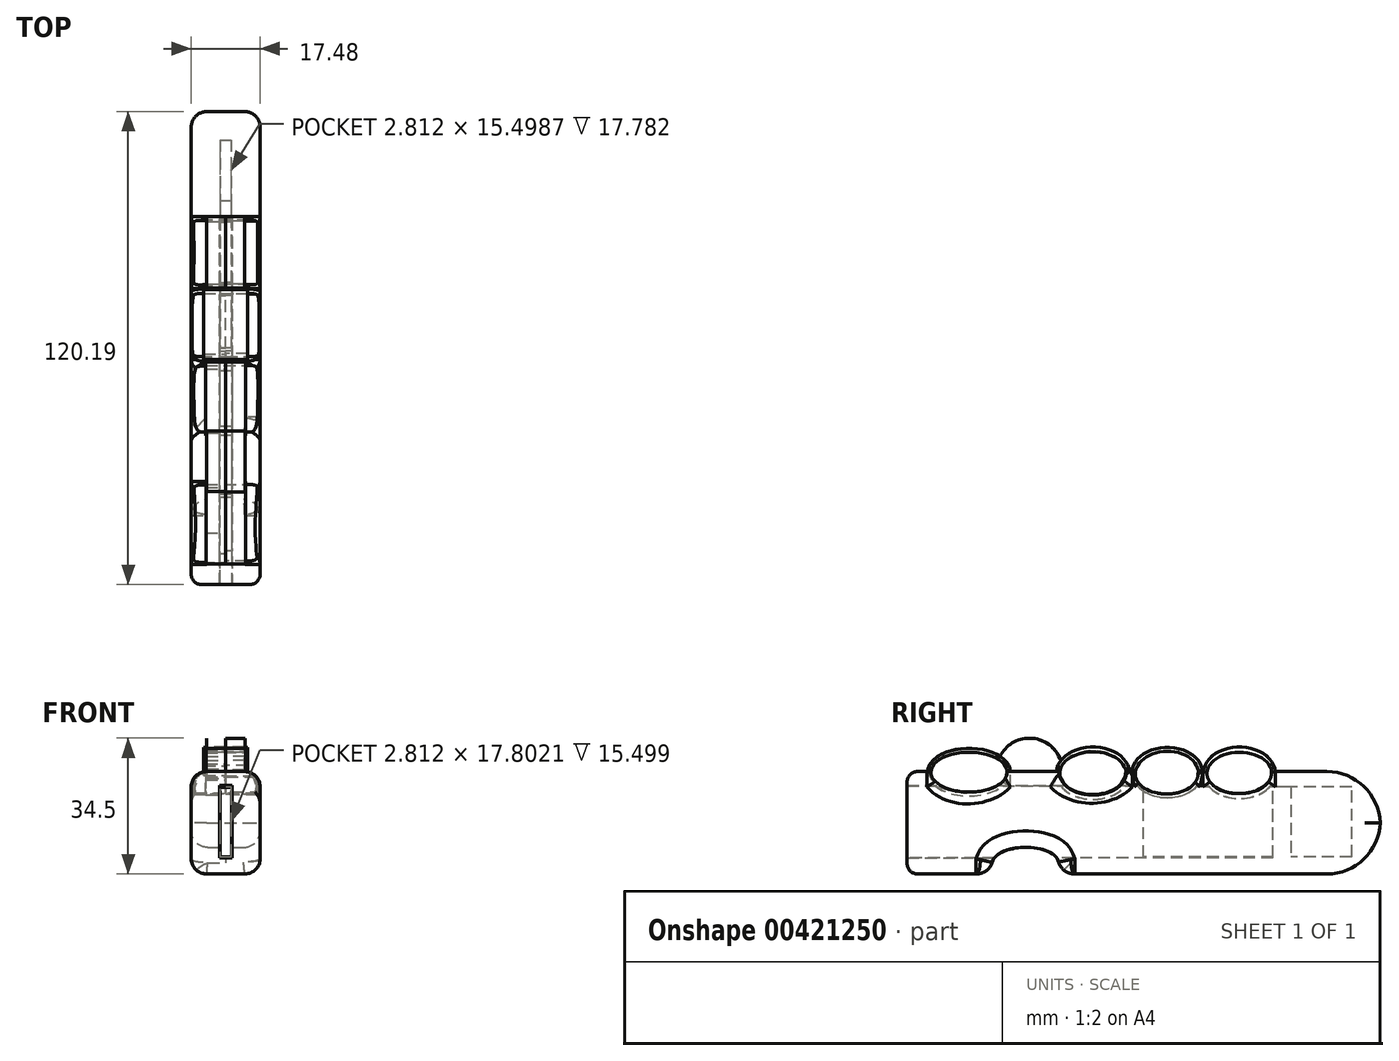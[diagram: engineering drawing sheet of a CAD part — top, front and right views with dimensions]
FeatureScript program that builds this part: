
annotation { "Feature Type Name" : "Feature", "Feature Type Description" : "" }
export const myFeature = defineFeature(function(context is Context, id is Id, definition is map)
    precondition{}
    {
        {
            var Q0;
            Q0=qCreatedBy(makeId("Top.planeOp"),FACE);
            var sketch = newSketch(context, id + "F0", { "sketchPlane" : qUnion([Q0])});
            skLineSegment(sketch, "E0.bottom", {"start": v(8.74, -60.1) * mm, "end": v(-8.74, -60.1) * mm});
            skLineSegment(sketch, "E0.top", {"start": v(8.74, 60.1) * mm, "end": v(-8.74, 60.1) * mm});
            skLineSegment(sketch, "E0.left", {"start": v(8.74, -60.1) * mm, "end": v(8.74, 60.1) * mm});
            skLineSegment(sketch, "E0.right", {"start": v(-8.74, -60.1) * mm, "end": v(-8.74, 60.1) * mm});
            skPoint(sketch, "E0.middle", {"position": v(0, 0) * mm});
            skSolve(sketch);
        }
        {
            var Q0;
            Q0=makeQuery(id+"F0.imprint","IMPRINT",FACE,{"disambiguationData":[TD([[makeQuery(id+"F0.imprint","IMPRINT",EDGE,{"derivedFrom":sQuery(id+"F0.wireOp",EDGE,"E0.bottom")}),-1.0]])]});
            extrude(context, id + "F1", {"entities" : qUnion([Q0]), "depth" : 26 * mm});
        }
        {
            var Q0;
            Q0=makeQuery(id+"F1.opExtrude","SWEPT_EDGE",EDGE,{"disambiguationData":[OSD([sQuery(id+"F0.wireOp",EDGE,"E0.bottom"),sQuery(id+"F0.wireOp",EDGE,"E0.left")])]});
            var Q1;
            Q1=makeQuery(id+"F1.opExtrude","SWEPT_EDGE",EDGE,{"disambiguationData":[OSD([sQuery(id+"F0.wireOp",EDGE,"E0.bottom"),sQuery(id+"F0.wireOp",EDGE,"E0.right")])]});
            var Q2;
            Q2=makeQuery(id+"F1.opExtrude","CAP_EDGE",EDGE,{"disambiguationData":[OSD([sQuery(id+"F0.wireOp",EDGE,"E0.bottom")])],"isStart":true});
            var Q3;
            Q3=makeQuery(id+"F1.opExtrude","CAP_EDGE",EDGE,{"disambiguationData":[OSD([sQuery(id+"F0.wireOp",EDGE,"E0.bottom")])],"isStart":false});
            fillet(context, id + "F2", {"entities" : qUnion([Q0, Q1, Q2, Q3]), "radius" : 2.66 * mm, "tangentPropagation" : true, "allowEdgeOverflow" : false});
        }
        {
            var Q0;
            Q0=makeQuery(id+"F1.opExtrude","SWEPT_FACE",FACE,{"disambiguationData":[OSD([sQuery(id+"F0.wireOp",EDGE,"E0.bottom")])]});
            var sketch = newSketch(context, id + "F3", { "sketchPlane" : qUnion([Q0])});
            skLineSegment(sketch, "E1.bottom", {"start": v(1.46, 22.1) * mm, "end": v(-1.46, 22.1) * mm});
            skLineSegment(sketch, "E1.top", {"start": v(1.46, 4.26) * mm, "end": v(-1.46, 4.26) * mm});
            skLineSegment(sketch, "E1.left", {"start": v(1.46, 22.1) * mm, "end": v(1.46, 4.26) * mm});
            skLineSegment(sketch, "E1.right", {"start": v(-1.46, 22.1) * mm, "end": v(-1.46, 4.26) * mm});
            skPoint(sketch, "E1.middle", {"position": v(0, 13.18) * mm});
            skSolve(sketch);
        }
        {
            var Q0;
            Q0=makeQuery(id+"F1.opExtrude","CAP_EDGE",EDGE,{"disambiguationData":[OSD([sQuery(id+"F0.wireOp",EDGE,"E0.top")])],"isStart":false});
            var Q1;
            Q1=makeQuery(id+"F1.opExtrude","CAP_EDGE",EDGE,{"disambiguationData":[OSD([sQuery(id+"F0.wireOp",EDGE,"E0.top")])],"isStart":true});
            fillet(context, id + "F4", {"entities" : qUnion([Q0, Q1]), "radius" : 13.52 * mm, "tangentPropagation" : true, "allowEdgeOverflow" : false});
        }
        {
            var Q0;
            Q0=makeQuery(id+"F4.opFillet","BLEND_EDGE",EDGE,{"blendedFrom":[makeQuery(id+"F1.opExtrude","CAP_EDGE",EDGE,{"disambiguationData":[OSD([sQuery(id+"F0.wireOp",EDGE,"E0.top")])],"isStart":true}),makeQuery(id+"F1.opExtrude","SWEPT_FACE",FACE,{"disambiguationData":[OSD([sQuery(id+"F0.wireOp",EDGE,"E0.right")])]})],"blendedInto":[makeQuery(id+"F1.opExtrude","SWEPT_FACE",FACE,{"disambiguationData":[OSD([sQuery(id+"F0.wireOp",EDGE,"E0.right")])]})]});
            var Q1;
            Q1=makeQuery(id+"F4.opFillet","BLEND_EDGE",EDGE,{"blendedFrom":[makeQuery(id+"F1.opExtrude","CAP_EDGE",EDGE,{"disambiguationData":[OSD([sQuery(id+"F0.wireOp",EDGE,"E0.top")])],"isStart":false}),makeQuery(id+"F1.opExtrude","SWEPT_FACE",FACE,{"disambiguationData":[OSD([sQuery(id+"F0.wireOp",EDGE,"E0.right")])]})],"blendedInto":[makeQuery(id+"F1.opExtrude","SWEPT_FACE",FACE,{"disambiguationData":[OSD([sQuery(id+"F0.wireOp",EDGE,"E0.right")])]})]});
            var Q2;
            Q2=makeQuery(id+"F4.opFillet","BLEND_EDGE",EDGE,{"blendedFrom":[makeQuery(id+"F1.opExtrude","CAP_EDGE",EDGE,{"disambiguationData":[OSD([sQuery(id+"F0.wireOp",EDGE,"E0.top")])],"isStart":false}),makeQuery(id+"F1.opExtrude","SWEPT_FACE",FACE,{"disambiguationData":[OSD([sQuery(id+"F0.wireOp",EDGE,"E0.left")])]})],"blendedInto":[makeQuery(id+"F1.opExtrude","SWEPT_FACE",FACE,{"disambiguationData":[OSD([sQuery(id+"F0.wireOp",EDGE,"E0.left")])]})]});
            var Q3;
            Q3=makeQuery(id+"F4.opFillet","BLEND_EDGE",EDGE,{"blendedFrom":[makeQuery(id+"F1.opExtrude","CAP_EDGE",EDGE,{"disambiguationData":[OSD([sQuery(id+"F0.wireOp",EDGE,"E0.top")])],"isStart":true}),makeQuery(id+"F1.opExtrude","SWEPT_FACE",FACE,{"disambiguationData":[OSD([sQuery(id+"F0.wireOp",EDGE,"E0.left")])]})],"blendedInto":[makeQuery(id+"F1.opExtrude","SWEPT_FACE",FACE,{"disambiguationData":[OSD([sQuery(id+"F0.wireOp",EDGE,"E0.left")])]})]});
            fillet(context, id + "F5", {"entities" : qUnion([Q0, Q1, Q2, Q3]), "radius" : 3.86 * mm, "tangentPropagation" : true, "allowEdgeOverflow" : false});
        }
        {
            var Q0;
            Q0=qCreatedBy(makeId("Right.planeOp"),FACE);
            var sketch = newSketch(context, id + "F6", { "sketchPlane" : qUnion([Q0])});
            skFitSpline(sketch, "E2", {"points": [v(-37.07, 26.03) * mm, v(-44.76, 21.99) * mm, v(-51.63, 25.96) * mm, v(-37.07, 26.03) * mm]});
            skSolve(sketch);
        }
        {
            var Q0;
            Q0=qCreatedBy(makeId("Right.planeOp"),FACE);
            var sketch = newSketch(context, id + "F7", { "sketchPlane" : qUnion([Q0])});
            skFitSpline(sketch, "E3", {"points": [v(-37.02, 26.06) * mm, v(-44.82, 21.98) * mm, v(-51.63, 25.93) * mm, v(-37.02, 26.06) * mm]});
            skSolve(sketch);
        }
        {
            var Q0;
            Q0 = qSketchRegion(id + "F6", true);
            extrude(context, id + "F8", {"entities" : qUnion([Q0]), "operationType" : NewBodyOperationType.REMOVE, "oppositeDirection" : true, "depth" : 25 * mm});
        }
        {
            var Q0;
            Q0 = qSketchRegion(id + "F7", true);
            extrude(context, id + "F9", {"entities" : qUnion([Q0]), "operationType" : NewBodyOperationType.REMOVE, "depth" : 25 * mm});
        }
        {
            var Q0;
            {var subQ0=sQuery(id+"F0.wireOp",EDGE,"E0.right");Q0=makeQuery(id+"F8.boolean.opBoolean","INTERSECT",EDGE,{"disambiguationData":[OD(0.0)],"derivedFrom":[makeQuery(id+"F5.opFillet","BLEND_FACE",FACE,{"disambiguationData":[OSD([subQ0]),TDD([makeQuery(id+"F1.opExtrude","CAP_EDGE",EDGE,{"disambiguationData":[OSD([subQ0])],"isStart":false})])]}),makeQuery(id+"F8.opExtrude","SWEPT_FACE",FACE,{"disambiguationData":[OSD([sQuery(id+"F6.wireOp",EDGE,"E2")])]})]});}
            var Q1;
            {var subQ0=sQuery(id+"F0.wireOp",EDGE,"E0.right");Q1=makeQuery(id+"F8.boolean.opBoolean","INTERSECT",EDGE,{"disambiguationData":[OD(1.0)],"derivedFrom":[makeQuery(id+"F5.opFillet","BLEND_FACE",FACE,{"disambiguationData":[OSD([subQ0]),TDD([makeQuery(id+"F1.opExtrude","CAP_EDGE",EDGE,{"disambiguationData":[OSD([subQ0])],"isStart":false})])]}),makeQuery(id+"F8.opExtrude","SWEPT_FACE",FACE,{"disambiguationData":[OSD([sQuery(id+"F6.wireOp",EDGE,"E2")])]})]});}
            fillet(context, id + "F10", {"entities" : qUnion([Q0, Q1]), "radius" : 4.2 * mm, "tangentPropagation" : true, "allowEdgeOverflow" : false});
        }
        {
            var Q0;
            {var subQ0=sQuery(id+"F0.wireOp",EDGE,"E0.left");Q0=makeQuery(id+"F9.boolean.opBoolean","INTERSECT",EDGE,{"disambiguationData":[OD(1.0)],"derivedFrom":[makeQuery(id+"F5.opFillet","BLEND_FACE",FACE,{"disambiguationData":[OSD([subQ0]),TDD([makeQuery(id+"F1.opExtrude","CAP_EDGE",EDGE,{"disambiguationData":[OSD([subQ0])],"isStart":false})])]}),makeQuery(id+"F9.opExtrude","SWEPT_FACE",FACE,{"disambiguationData":[OSD([sQuery(id+"F7.wireOp",EDGE,"E3")])]})]});}
            var Q1;
            {var subQ0=sQuery(id+"F0.wireOp",EDGE,"E0.left");Q1=makeQuery(id+"F9.boolean.opBoolean","INTERSECT",EDGE,{"disambiguationData":[OD(0.0)],"derivedFrom":[makeQuery(id+"F5.opFillet","BLEND_FACE",FACE,{"disambiguationData":[OSD([subQ0]),TDD([makeQuery(id+"F1.opExtrude","CAP_EDGE",EDGE,{"disambiguationData":[OSD([subQ0])],"isStart":false})])]}),makeQuery(id+"F9.opExtrude","SWEPT_FACE",FACE,{"disambiguationData":[OSD([sQuery(id+"F7.wireOp",EDGE,"E3")])]})]});}
            fillet(context, id + "F11", {"entities" : qUnion([Q0, Q1]), "radius" : 4.2 * mm, "tangentPropagation" : true, "allowEdgeOverflow" : false});
        }
        {
            var Q0;
            Q0=makeQuery(id+"F3.imprint","IMPRINT",FACE,{"disambiguationData":[TD([[makeQuery(id+"F3.imprint","IMPRINT",EDGE,{"derivedFrom":sQuery(id+"F3.wireOp",EDGE,"E1.bottom")}),-1.0]])]});
            var sketch = newSketch(context, id + "F12", { "sketchPlane" : qUnion([Q0])});
            skLineSegment(sketch, "E4.bottom", {"start": v(-1.6, 4.04) * mm, "end": v(1.6, 4.04) * mm});
            skLineSegment(sketch, "E4.top", {"start": v(-1.6, 22.35) * mm, "end": v(1.6, 22.35) * mm});
            skLineSegment(sketch, "E4.left", {"start": v(-1.6, 4.04) * mm, "end": v(-1.6, 22.35) * mm});
            skLineSegment(sketch, "E4.right", {"start": v(1.6, 4.04) * mm, "end": v(1.6, 22.35) * mm});
            skPoint(sketch, "E4.middle", {"position": v(0, 13.2) * mm});
            skSolve(sketch);
        }
        {
            var Q0;
            Q0 = qSketchRegion(id + "F12", true);
            extrude(context, id + "F13", {"entities" : qUnion([Q0]), "operationType" : NewBodyOperationType.REMOVE, "oppositeDirection" : true, "depth" : 93 * mm});
        }
        {
            var Q0;
            Q0=makeQuery(id+"F3.imprint","IMPRINT",FACE,{"disambiguationData":[TD([[makeQuery(id+"F3.imprint","IMPRINT",EDGE,{"derivedFrom":sQuery(id+"F3.wireOp",EDGE,"E1.bottom")}),1.0]])]});
            var sketch = newSketch(context, id + "F14", { "sketchPlane" : qUnion([Q0])});
            skLineSegment(sketch, "E5.bottom", {"start": v(-1.4, 4.37) * mm, "end": v(1.4, 4.37) * mm});
            skLineSegment(sketch, "E5.top", {"start": v(-1.4, 22.17) * mm, "end": v(1.4, 22.17) * mm});
            skLineSegment(sketch, "E5.left", {"start": v(-1.4, 4.37) * mm, "end": v(-1.4, 22.17) * mm});
            skLineSegment(sketch, "E5.right", {"start": v(1.4, 4.37) * mm, "end": v(1.4, 22.17) * mm});
            skPoint(sketch, "E5.middle", {"position": v(0, 13.27) * mm});
            skSolve(sketch);
        }
        {
            var Q0;
            Q0 = qSketchRegion(id + "F14", true);
            extrude(context, id + "F15", {"entities" : qUnion([Q0]), "operationType" : NewBodyOperationType.REMOVE, "oppositeDirection" : true, "depth" : 113 * mm});
        }
        {
            var Q0;
            Q0=qCreatedBy(makeId("Right.planeOp"),FACE);
            var sketch = newSketch(context, id + "F16", { "sketchPlane" : qUnion([Q0])});
            skFitSpline(sketch, "E6", {"points": [v(-21.94, 3.88) * mm, v(-30.28, -6.1) * mm, v(-38.08, 3.82) * mm, v(-21.94, 3.88) * mm]});
            skSolve(sketch);
        }
        {
            var Q0;
            Q0=qCreatedBy(makeId("Right.planeOp"),FACE);
            var sketch = newSketch(context, id + "F17", { "sketchPlane" : qUnion([Q0])});
            skFitSpline(sketch, "E7", {"points": [v(-21.92, 3.9) * mm, v(-30.28, -6.09) * mm, v(-38.07, 3.82) * mm, v(-21.92, 3.9) * mm]});
            skSolve(sketch);
        }
        {
            var Q0;
            Q0 = qSketchRegion(id + "F17", true);
            extrude(context, id + "F18", {"entities" : qUnion([Q0]), "operationType" : NewBodyOperationType.REMOVE, "oppositeDirection" : true, "depth" : 25 * mm});
        }
        {
            var Q0;
            Q0 = qSketchRegion(id + "F16", true);
            extrude(context, id + "F19", {"entities" : qUnion([Q0]), "operationType" : NewBodyOperationType.REMOVE, "depth" : 25 * mm});
        }
        {
            var Q0;
            Q0=makeQuery(id+"F18.boolean.opBoolean","INTERSECT",EDGE,{"derivedFrom":[makeQuery(id+"F1.opExtrude","SWEPT_FACE",FACE,{"disambiguationData":[OSD([sQuery(id+"F0.wireOp",EDGE,"E0.right")])]}),makeQuery(id+"F18.opExtrude","SWEPT_FACE",FACE,{"disambiguationData":[OSD([sQuery(id+"F17.wireOp",EDGE,"E7")])]})]});
            var Q1;
            Q1=makeQuery(id+"F19.boolean.opBoolean","INTERSECT",EDGE,{"derivedFrom":[makeQuery(id+"F1.opExtrude","SWEPT_FACE",FACE,{"disambiguationData":[OSD([sQuery(id+"F0.wireOp",EDGE,"E0.left")])]}),makeQuery(id+"F19.opExtrude","SWEPT_FACE",FACE,{"disambiguationData":[OSD([sQuery(id+"F16.wireOp",EDGE,"E6")])]})]});
            fillet(context, id + "F20", {"entities" : qUnion([Q0, Q1]), "radius" : 4.2 * mm, "allowEdgeOverflow" : false});
        }
        {
            var Q0;
            Q0=makeQuery(id+"F18.boolean.opBoolean","INTERSECT",EDGE,{"disambiguationData":[OD(0.0)],"derivedFrom":[makeQuery(id+"F1.opExtrude","CAP_FACE",FACE,{"disambiguationData":[OSD([sQuery(id+"F0.wireOp",EDGE,"E0.bottom"),sQuery(id+"F0.wireOp",EDGE,"E0.top"),sQuery(id+"F0.wireOp",EDGE,"E0.left"),sQuery(id+"F0.wireOp",EDGE,"E0.right")])],"isStart":true}),makeQuery(id+"F18.opExtrude","SWEPT_FACE",FACE,{"disambiguationData":[OSD([sQuery(id+"F17.wireOp",EDGE,"E7")])]})]});
            var Q1;
            Q1=makeQuery(id+"F19.boolean.opBoolean","INTERSECT",EDGE,{"disambiguationData":[OD(1.0)],"derivedFrom":[makeQuery(id+"F1.opExtrude","CAP_FACE",FACE,{"disambiguationData":[OSD([sQuery(id+"F0.wireOp",EDGE,"E0.bottom"),sQuery(id+"F0.wireOp",EDGE,"E0.top"),sQuery(id+"F0.wireOp",EDGE,"E0.left"),sQuery(id+"F0.wireOp",EDGE,"E0.right")])],"isStart":true}),makeQuery(id+"F19.opExtrude","SWEPT_FACE",FACE,{"disambiguationData":[OSD([sQuery(id+"F16.wireOp",EDGE,"E6")])]})]});
            fillet(context, id + "F21", {"entities" : qUnion([Q0, Q1]), "radius" : 4.2 * mm, "tangentPropagation" : true, "allowEdgeOverflow" : false});
        }
        {
            var Q0;
            Q0=qCreatedBy(makeId("Right.planeOp"),FACE);
            var sketch = newSketch(context, id + "F22", { "sketchPlane" : qUnion([Q0])});
            skLineSegment(sketch, "E8.bottom", {"start": v(-37.4, 24.67) * mm, "end": v(-20.56, 24.67) * mm});
            skLineSegment(sketch, "E8.top", {"start": v(-37.4, 34.49) * mm, "end": v(-20.56, 34.49) * mm});
            skLineSegment(sketch, "E8.left", {"start": v(-37.4, 24.67) * mm, "end": v(-37.4, 34.49) * mm});
            skLineSegment(sketch, "E8.right", {"start": v(-20.56, 24.67) * mm, "end": v(-20.56, 34.49) * mm});
            skPoint(sketch, "E8.middle", {"position": v(-28.98, 29.58) * mm});
            skSolve(sketch);
        }
        {
            var Q0;
            Q0=qCreatedBy(makeId("Right.planeOp"),FACE);
            var sketch = newSketch(context, id + "F23", { "sketchPlane" : qUnion([Q0])});
            skLineSegment(sketch, "E9.bottom", {"start": v(-37.41, 24.63) * mm, "end": v(-20.61, 24.63) * mm});
            skLineSegment(sketch, "E9.top", {"start": v(-37.41, 34.5) * mm, "end": v(-20.61, 34.5) * mm});
            skLineSegment(sketch, "E9.left", {"start": v(-37.41, 24.63) * mm, "end": v(-37.41, 34.5) * mm});
            skLineSegment(sketch, "E9.right", {"start": v(-20.61, 24.63) * mm, "end": v(-20.61, 34.5) * mm});
            skPoint(sketch, "E9.middle", {"position": v(-29.01, 29.57) * mm});
            skSolve(sketch);
        }
        {
            var Q0;
            Q0 = qSketchRegion(id + "F23", true);
            extrude(context, id + "F24", {"entities" : qUnion([Q0]), "operationType" : NewBodyOperationType.ADD, "depth" : 4.9 * mm});
        }
        {
            var Q0;
            Q0 = qSketchRegion(id + "F22", true);
            extrude(context, id + "F25", {"entities" : qUnion([Q0]), "operationType" : NewBodyOperationType.ADD, "oppositeDirection" : true, "depth" : 4.9 * mm});
        }
        {
            var Q0;
            Q0=makeQuery(id+"F25.opExtrude","SWEPT_EDGE",EDGE,{"disambiguationData":[OSD([sQuery(id+"F22.wireOp",EDGE,"E8.top"),sQuery(id+"F22.wireOp",EDGE,"E8.right")])]});
            var Q1;
            Q1=makeQuery(id+"F25.opExtrude","SWEPT_EDGE",EDGE,{"disambiguationData":[OSD([sQuery(id+"F22.wireOp",EDGE,"E8.top"),sQuery(id+"F22.wireOp",EDGE,"E8.left")])]});
            var Q2;
            Q2=makeQuery(id+"F24.opExtrude","SWEPT_EDGE",EDGE,{"disambiguationData":[OSD([sQuery(id+"F23.wireOp",EDGE,"E9.top"),sQuery(id+"F23.wireOp",EDGE,"E9.left")])]});
            fillet(context, id + "F26", {"entities" : qUnion([Q0, Q1, Q2]), "radius" : 8.43 * mm, "tangentPropagation" : true, "allowEdgeOverflow" : false});
        }
        {
            var Q0;
            Q0=makeQuery(id+"F24.opExtrude","SWEPT_EDGE",EDGE,{"disambiguationData":[OSD([sQuery(id+"F23.wireOp",EDGE,"E9.top"),sQuery(id+"F23.wireOp",EDGE,"E9.right")])]});
            fillet(context, id + "F27", {"entities" : qUnion([Q0]), "radius" : 8.43 * mm, "tangentPropagation" : true, "allowEdgeOverflow" : false});
        }
        {
            var Q0;
            Q0=qCreatedBy(makeId("Right.planeOp"),FACE);
            var sketch = newSketch(context, id + "F28", { "sketchPlane" : qUnion([Q0])});
            skFitSpline(sketch, "E10", {"points": [v(-6.03, 26.03) * mm, v(-13.3, 22.09) * mm, v(-20.6, 26.14) * mm, v(-6.03, 26.03) * mm]});
            skSolve(sketch);
        }
        {
            var Q0;
            Q0=qCreatedBy(makeId("Right.planeOp"),FACE);
            var sketch = newSketch(context, id + "F29", { "sketchPlane" : qUnion([Q0])});
            skFitSpline(sketch, "E11", {"points": [v(-20.59, 26.16) * mm, v(-13.32, 22.08) * mm, v(-6.05, 26.04) * mm, v(-20.59, 26.16) * mm]});
            skSolve(sketch);
        }
        {
            var Q0;
            Q0 = qSketchRegion(id + "F28", true);
            extrude(context, id + "F30", {"entities" : qUnion([Q0]), "operationType" : NewBodyOperationType.REMOVE, "oppositeDirection" : true, "depth" : 25 * mm});
        }
        {
            var Q0;
            Q0 = qSketchRegion(id + "F29", true);
            extrude(context, id + "F31", {"entities" : qUnion([Q0]), "operationType" : NewBodyOperationType.REMOVE, "depth" : 25 * mm});
        }
        {
            var Q0;
            {var subQ0=sQuery(id+"F0.wireOp",EDGE,"E0.left");var subQ1=sQuery(id+"F0.wireOp",EDGE,"E0.right");var subQ2=sQuery(id+"F0.wireOp",EDGE,"E0.top");var subQ4=sQuery(id+"F7.wireOp",EDGE,"E3");Q0=makeQuery(id+"F30.boolean.opBoolean","INTERSECT",EDGE,{"derivedFrom":[makeQuery(id+"F9.boolean.opBoolean","SPLIT",FACE,{"disambiguationData":[TD([makeQuery(id+"F9.opExtrude","CAP_FACE",FACE,{"disambiguationData":[OSD([subQ4])],"isStart":true})])],"derivedFrom":makeQuery(id+"F1.opExtrude","CAP_FACE",FACE,{"disambiguationData":[OSD([sQuery(id+"F0.wireOp",EDGE,"E0.bottom"),subQ2,subQ0,subQ1])],"isStart":false})}),makeQuery(id+"F30.opExtrude","SWEPT_FACE",FACE,{"disambiguationData":[OSD([sQuery(id+"F28.wireOp",EDGE,"E10")])]})]});}
            fillet(context, id + "F32", {"entities" : qUnion([Q0]), "radius" : 4.13 * mm, "tangentPropagation" : true, "allowEdgeOverflow" : false});
        }
        {
            var Q0;
            {var subQ0=sQuery(id+"F0.wireOp",EDGE,"E0.left");var subQ2=sQuery(id+"F0.wireOp",EDGE,"E0.top");var subQ3=makeQuery(id+"F1.opExtrude","CAP_EDGE",EDGE,{"disambiguationData":[OSD([subQ2])],"isStart":false});Q0=makeQuery(id+"F31.boolean.opBoolean","INTERSECT",EDGE,{"disambiguationData":[OD(0.0)],"derivedFrom":[makeQuery(id+"F9.boolean.opBoolean","SPLIT",FACE,{"disambiguationData":[TD([makeQuery(id+"F4.opFillet","BLEND_FACE",FACE,{"disambiguationData":[OSD([subQ2]),TDD([subQ3])]})])],"derivedFrom":makeQuery(id+"F5.opFillet","BLEND_FACE",FACE,{"disambiguationData":[OSD([subQ0]),TDD([makeQuery(id+"F1.opExtrude","CAP_EDGE",EDGE,{"disambiguationData":[OSD([subQ0])],"isStart":false})])]})}),makeQuery(id+"F31.opExtrude","SWEPT_FACE",FACE,{"disambiguationData":[OSD([sQuery(id+"F29.wireOp",EDGE,"E11")])]})]});}
            fillet(context, id + "F33", {"entities" : qUnion([Q0]), "radius" : 4.13 * mm, "tangentPropagation" : true, "allowEdgeOverflow" : false});
        }
        {
            var Q0;
            Q0=qCreatedBy(makeId("Right.planeOp"),FACE);
            var sketch = newSketch(context, id + "F34", { "sketchPlane" : qUnion([Q0])});
            skFitSpline(sketch, "E12", {"points": [v(12.7, 26.02) * mm, v(6.1, 22.11) * mm, v(-0.72, 25.97) * mm, v(12.7, 26.02) * mm]});
            skSolve(sketch);
        }
        {
            var Q0;
            Q0=qCreatedBy(makeId("Right.planeOp"),FACE);
            var sketch = newSketch(context, id + "F35", { "sketchPlane" : qUnion([Q0])});
            skFitSpline(sketch, "E13", {"points": [v(12.7, 26.03) * mm, v(6.1, 22.11) * mm, v(-0.72, 25.97) * mm, v(12.7, 26.03) * mm]});
            skSolve(sketch);
        }
        {
            var Q0;
            Q0 = qSketchRegion(id + "F34", true);
            extrude(context, id + "F36", {"entities" : qUnion([Q0]), "operationType" : NewBodyOperationType.REMOVE, "oppositeDirection" : true, "depth" : 25 * mm});
        }
        {
            var Q0;
            Q0 = qSketchRegion(id + "F35", true);
            extrude(context, id + "F37", {"entities" : qUnion([Q0]), "operationType" : NewBodyOperationType.REMOVE, "depth" : 25 * mm});
        }
        {
            var Q0;
            {var subQ0=sQuery(id+"F0.wireOp",EDGE,"E0.left");var subQ2=sQuery(id+"F0.wireOp",EDGE,"E0.top");var subQ3=makeQuery(id+"F1.opExtrude","CAP_EDGE",EDGE,{"disambiguationData":[OSD([subQ2])],"isStart":false});var subQ5=makeQuery(id+"F4.opFillet","BLEND_FACE",FACE,{"disambiguationData":[OSD([subQ2]),TDD([subQ3])]});Q0=makeQuery(id+"F37.boolean.opBoolean","INTERSECT",EDGE,{"disambiguationData":[OD(1.0)],"derivedFrom":[makeQuery(id+"F31.boolean.opBoolean","SPLIT",FACE,{"disambiguationData":[TD([subQ5])],"derivedFrom":makeQuery(id+"F9.boolean.opBoolean","SPLIT",FACE,{"disambiguationData":[TD([subQ5])],"derivedFrom":makeQuery(id+"F5.opFillet","BLEND_FACE",FACE,{"disambiguationData":[OSD([subQ0]),TDD([makeQuery(id+"F1.opExtrude","CAP_EDGE",EDGE,{"disambiguationData":[OSD([subQ0])],"isStart":false})])]})})}),makeQuery(id+"F37.opExtrude","SWEPT_FACE",FACE,{"disambiguationData":[OSD([sQuery(id+"F35.wireOp",EDGE,"E13")])]})]});}
            var Q1;
            {var subQ0=sQuery(id+"F0.wireOp",EDGE,"E0.top");var subQ1=makeQuery(id+"F1.opExtrude","CAP_EDGE",EDGE,{"disambiguationData":[OSD([subQ0])],"isStart":false});var subQ2=makeQuery(id+"F4.opFillet","BLEND_FACE",FACE,{"disambiguationData":[OSD([subQ0]),TDD([subQ1])]});var subQ3=sQuery(id+"F0.wireOp",EDGE,"E0.right");Q1=makeQuery(id+"F36.boolean.opBoolean","INTERSECT",EDGE,{"disambiguationData":[OD(1.0)],"derivedFrom":[makeQuery(id+"F30.boolean.opBoolean","SPLIT",FACE,{"disambiguationData":[TD([subQ2])],"derivedFrom":makeQuery(id+"F8.boolean.opBoolean","SPLIT",FACE,{"disambiguationData":[TD([subQ2])],"derivedFrom":makeQuery(id+"F5.opFillet","BLEND_FACE",FACE,{"disambiguationData":[OSD([subQ3]),TDD([makeQuery(id+"F1.opExtrude","CAP_EDGE",EDGE,{"disambiguationData":[OSD([subQ3])],"isStart":false})])]})})}),makeQuery(id+"F36.opExtrude","SWEPT_FACE",FACE,{"disambiguationData":[OSD([sQuery(id+"F34.wireOp",EDGE,"E12")])]})]});}
            fillet(context, id + "F38", {"entities" : qUnion([Q0, Q1]), "radius" : 2.92 * mm, "tangentPropagation" : true, "allowEdgeOverflow" : false});
        }
        {
            var Q0;
            Q0=qCreatedBy(makeId("Right.planeOp"),FACE);
            var sketch = newSketch(context, id + "F39", { "sketchPlane" : qUnion([Q0])});
            skLineSegment(sketch, "E14.bottom", {"start": v(18.16, 27.18) * mm, "end": v(30.41, 27.18) * mm});
            skLineSegment(sketch, "E14.top", {"start": v(18.16, 28.34) * mm, "end": v(30.41, 28.34) * mm});
            skLineSegment(sketch, "E14.left", {"start": v(18.16, 27.18) * mm, "end": v(18.16, 28.34) * mm});
            skLineSegment(sketch, "E14.right", {"start": v(30.41, 27.18) * mm, "end": v(30.41, 28.34) * mm});
            skPoint(sketch, "E14.middle", {"position": v(24.29, 27.76) * mm});
            skFitSpline(sketch, "E15", {"points": [v(30.41, 26) * mm, v(24.29, 22.15) * mm, v(18.16, 25.93) * mm, v(30.41, 26) * mm]});
            skSolve(sketch);
        }
        {
            var Q0;
            Q0=qCreatedBy(makeId("Right.planeOp"),FACE);
            var sketch = newSketch(context, id + "F40", { "sketchPlane" : qUnion([Q0])});
            skFitSpline(sketch, "E16", {"points": [v(30.41, 26) * mm, v(24.29, 22.15) * mm, v(18.16, 25.93) * mm, v(30.41, 26) * mm]});
            skSolve(sketch);
        }
        {
            var Q0;
            Q0 = qSketchRegion(id + "F39", true);
            extrude(context, id + "F41", {"entities" : qUnion([Q0]), "operationType" : NewBodyOperationType.REMOVE, "oppositeDirection" : true, "depth" : 25 * mm});
        }
        {
            var Q0;
            Q0 = qSketchRegion(id + "F40", true);
            extrude(context, id + "F42", {"entities" : qUnion([Q0]), "operationType" : NewBodyOperationType.REMOVE, "depth" : 25 * mm});
        }
        {
            var Q0;
            {var subQ0=sQuery(id+"F0.wireOp",EDGE,"E0.top");var subQ1=makeQuery(id+"F1.opExtrude","CAP_EDGE",EDGE,{"disambiguationData":[OSD([subQ0])],"isStart":false});var subQ2=makeQuery(id+"F4.opFillet","BLEND_FACE",FACE,{"disambiguationData":[OSD([subQ0]),TDD([subQ1])]});var subQ3=sQuery(id+"F0.wireOp",EDGE,"E0.right");Q0=makeQuery(id+"F41.boolean.opBoolean","INTERSECT",EDGE,{"derivedFrom":[makeQuery(id+"F36.boolean.opBoolean","SPLIT",FACE,{"disambiguationData":[TD([subQ2])],"derivedFrom":makeQuery(id+"F30.boolean.opBoolean","SPLIT",FACE,{"disambiguationData":[TD([subQ2])],"derivedFrom":makeQuery(id+"F8.boolean.opBoolean","SPLIT",FACE,{"disambiguationData":[TD([subQ2])],"derivedFrom":makeQuery(id+"F5.opFillet","BLEND_FACE",FACE,{"disambiguationData":[OSD([subQ3]),TDD([makeQuery(id+"F1.opExtrude","CAP_EDGE",EDGE,{"disambiguationData":[OSD([subQ3])],"isStart":false})])]})})})}),makeQuery(id+"F41.opExtrude","SWEPT_FACE",FACE,{"disambiguationData":[OSD([sQuery(id+"F39.wireOp",EDGE,"E15")])]})]});}
            var Q1;
            {var subQ0=sQuery(id+"F0.wireOp",EDGE,"E0.left");var subQ2=sQuery(id+"F0.wireOp",EDGE,"E0.top");var subQ3=makeQuery(id+"F1.opExtrude","CAP_EDGE",EDGE,{"disambiguationData":[OSD([subQ2])],"isStart":false});var subQ5=makeQuery(id+"F4.opFillet","BLEND_FACE",FACE,{"disambiguationData":[OSD([subQ2]),TDD([subQ3])]});Q1=makeQuery(id+"F42.boolean.opBoolean","INTERSECT",EDGE,{"derivedFrom":[makeQuery(id+"F37.boolean.opBoolean","SPLIT",FACE,{"disambiguationData":[TD([subQ5])],"derivedFrom":makeQuery(id+"F31.boolean.opBoolean","SPLIT",FACE,{"disambiguationData":[TD([subQ5])],"derivedFrom":makeQuery(id+"F9.boolean.opBoolean","SPLIT",FACE,{"disambiguationData":[TD([subQ5])],"derivedFrom":makeQuery(id+"F5.opFillet","BLEND_FACE",FACE,{"disambiguationData":[OSD([subQ0]),TDD([makeQuery(id+"F1.opExtrude","CAP_EDGE",EDGE,{"disambiguationData":[OSD([subQ0])],"isStart":false})])]})})})}),makeQuery(id+"F42.opExtrude","SWEPT_FACE",FACE,{"disambiguationData":[OSD([sQuery(id+"F40.wireOp",EDGE,"E16")])]})]});}
            fillet(context, id + "F43", {"entities" : qUnion([Q0, Q1]), "radius" : 4 * mm, "tangentPropagation" : true, "allowEdgeOverflow" : false});
        }
        {
            var Q0;
            Q0=qCreatedBy(makeId("Right.planeOp"),FACE);
            var sketch = newSketch(context, id + "F44", { "sketchPlane" : qUnion([Q0])});
            skEllipse(sketch, "E17", {"center": v(24.34, 25.69) * mm, "majorRadius": 9.12 * mm, "minorRadius": 6.56 * mm, "majorAxis": v(-1, 0)});
            skSolve(sketch);
        }
        {
            var Q0;
            Q0 = qSketchRegion(id + "F44", true);
            extrude(context, id + "F45", {"entities" : qUnion([Q0]), "operationType" : NewBodyOperationType.ADD, "depth" : 4.8 * mm});
        }
        {
            var Q0;
            Q0=qCreatedBy(makeId("Right.planeOp"),FACE);
            var sketch = newSketch(context, id + "F46", { "sketchPlane" : qUnion([Q0])});
            skEllipse(sketch, "E18", {"center": v(24.34, 25.71) * mm, "majorRadius": 9.12 * mm, "minorRadius": 6.56 * mm, "majorAxis": v(-1, 0)});
            skSolve(sketch);
        }
        {
            var Q0;
            Q0 = qSketchRegion(id + "F46", true);
            extrude(context, id + "F47", {"entities" : qUnion([Q0]), "operationType" : NewBodyOperationType.ADD, "oppositeDirection" : true, "depth" : 4.8 * mm});
        }
        {
            var Q0;
            Q0=qCreatedBy(makeId("Right.planeOp"),FACE);
            var sketch = newSketch(context, id + "F48", { "sketchPlane" : qUnion([Q0])});
            skEllipse(sketch, "E19", {"center": v(6.01, 25.77) * mm, "majorRadius": 8.93 * mm, "minorRadius": 6.39 * mm, "majorAxis": v(-1, 0)});
            skSolve(sketch);
        }
        {
            var Q0;
            Q0=qCreatedBy(makeId("Right.planeOp"),FACE);
            var sketch = newSketch(context, id + "F49", { "sketchPlane" : qUnion([Q0])});
            skEllipse(sketch, "E20", {"center": v(6.02, 25.77) * mm, "majorRadius": 8.93 * mm, "minorRadius": 6.39 * mm, "majorAxis": v(-1, 0)});
            skSolve(sketch);
        }
        {
            var Q0;
            Q0 = qSketchRegion(id + "F48", true);
            extrude(context, id + "F50", {"entities" : qUnion([Q0]), "operationType" : NewBodyOperationType.ADD, "depth" : 5.6 * mm});
        }
        {
            var Q0;
            Q0 = qSketchRegion(id + "F49", true);
            extrude(context, id + "F51", {"entities" : qUnion([Q0]), "operationType" : NewBodyOperationType.ADD, "oppositeDirection" : true, "depth" : 5.6 * mm});
        }
        {
            var Q0;
            Q0=makeQuery(id+"F51.opExtrude","CAP_FACE",FACE,{"disambiguationData":[OSD([sQuery(id+"F49.wireOp",EDGE,"E20")])],"isStart":false});
            var sketch = newSketch(context, id + "F52", { "sketchPlane" : qUnion([Q0])});
            skEllipse(sketch, "E21", {"center": v(-6.02, 25.77) * mm, "majorRadius": 7.88 * mm, "minorRadius": 5.4 * mm, "majorAxis": v(1, 0)});
            skSolve(sketch);
        }
        {
            var Q0;
            Q0 = qSketchRegion(id + "F52", true);
            extrude(context, id + "F53", {"entities" : qUnion([Q0]), "operationType" : NewBodyOperationType.REMOVE, "oppositeDirection" : true, "depth" : 25 * mm});
        }
        {
            var Q0;
            Q0=makeQuery(id+"F47.opExtrude","CAP_FACE",FACE,{"disambiguationData":[OSD([sQuery(id+"F46.wireOp",EDGE,"E18")])],"isStart":false});
            var sketch = newSketch(context, id + "F54", { "sketchPlane" : qUnion([Q0])});
            skEllipse(sketch, "E22", {"center": v(-24.34, 25.71) * mm, "majorRadius": 8.18 * mm, "minorRadius": 5.18 * mm, "majorAxis": v(1, 0)});
            skSolve(sketch);
        }
        {
            var Q0;
            Q0 = qSketchRegion(id + "F54", true);
            extrude(context, id + "F55", {"entities" : qUnion([Q0]), "operationType" : NewBodyOperationType.REMOVE, "oppositeDirection" : true, "depth" : 25 * mm});
        }
        {
            var Q0;
            Q0=qCreatedBy(makeId("Right.planeOp"),FACE);
            var sketch = newSketch(context, id + "F56", { "sketchPlane" : qUnion([Q0])});
            skEllipse(sketch, "E23", {"center": v(-12.87, 25.6) * mm, "majorRadius": 9.33 * mm, "minorRadius": 6.65 * mm, "majorAxis": v(-1, 0)});
            skSolve(sketch);
        }
        {
            var Q0;
            Q0=qCreatedBy(makeId("Right.planeOp"),FACE);
            var sketch = newSketch(context, id + "F57", { "sketchPlane" : qUnion([Q0])});
            skEllipse(sketch, "E24", {"center": v(-12.87, 25.56) * mm, "majorRadius": 9.33 * mm, "minorRadius": 6.65 * mm, "majorAxis": v(-1, 0)});
            skSolve(sketch);
        }
        {
            var Q0;
            Q0 = qSketchRegion(id + "F56", true);
            extrude(context, id + "F58", {"entities" : qUnion([Q0]), "operationType" : NewBodyOperationType.ADD, "depth" : 5.1 * mm});
        }
        {
            var Q0;
            Q0 = qSketchRegion(id + "F57", true);
            extrude(context, id + "F59", {"entities" : qUnion([Q0]), "operationType" : NewBodyOperationType.ADD, "oppositeDirection" : true, "depth" : 5.1 * mm});
        }
        {
            var Q0;
            Q0=makeQuery(id+"F59.opExtrude","CAP_FACE",FACE,{"disambiguationData":[OSD([sQuery(id+"F57.wireOp",EDGE,"E24")])],"isStart":false});
            var sketch = newSketch(context, id + "F60", { "sketchPlane" : qUnion([Q0])});
            skEllipse(sketch, "E25", {"center": v(12.87, 25.56) * mm, "majorRadius": 8.44 * mm, "minorRadius": 5.5 * mm, "majorAxis": v(1, 0)});
            skSolve(sketch);
        }
        {
            var Q0;
            Q0 = qSketchRegion(id + "F60", true);
            extrude(context, id + "F61", {"entities" : qUnion([Q0]), "operationType" : NewBodyOperationType.REMOVE, "oppositeDirection" : true, "depth" : 25 * mm});
        }
        {
            var Q0;
            Q0=qCreatedBy(makeId("Right.planeOp"),FACE);
            var sketch = newSketch(context, id + "F62", { "sketchPlane" : qUnion([Q0])});
            skEllipse(sketch, "E26", {"center": v(-44.35, 25.86) * mm, "majorRadius": 10.52 * mm, "minorRadius": 6.06 * mm, "majorAxis": v(-1, 0)});
            skSolve(sketch);
        }
        {
            var Q0;
            Q0=qCreatedBy(makeId("Right.planeOp"),FACE);
            var sketch = newSketch(context, id + "F63", { "sketchPlane" : qUnion([Q0])});
            skEllipse(sketch, "E27", {"center": v(-44.36, 25.86) * mm, "majorRadius": 10.52 * mm, "minorRadius": 6.06 * mm, "majorAxis": v(-1, 0)});
            skSolve(sketch);
        }
        {
            var Q0;
            Q0 = qSketchRegion(id + "F62", true);
            extrude(context, id + "F64", {"entities" : qUnion([Q0]), "operationType" : NewBodyOperationType.ADD, "depth" : 5 * mm});
        }
        {
            var Q0;
            Q0 = qSketchRegion(id + "F63", true);
            extrude(context, id + "F65", {"entities" : qUnion([Q0]), "operationType" : NewBodyOperationType.ADD, "oppositeDirection" : true, "depth" : 5 * mm});
        }
        {
            var Q0;
            Q0=makeQuery(id+"F65.opExtrude","CAP_FACE",FACE,{"disambiguationData":[OSD([sQuery(id+"F63.wireOp",EDGE,"E27")])],"isStart":false});
            var sketch = newSketch(context, id + "F66", { "sketchPlane" : qUnion([Q0])});
            skEllipse(sketch, "E28", {"center": v(44.36, 25.86) * mm, "majorRadius": 9.7 * mm, "minorRadius": 5.06 * mm, "majorAxis": v(1, 0)});
            skSolve(sketch);
        }
        {
            var Q0;
            Q0 = qSketchRegion(id + "F66", true);
            extrude(context, id + "F67", {"entities" : qUnion([Q0]), "operationType" : NewBodyOperationType.REMOVE, "oppositeDirection" : true, "depth" : 25 * mm});
        }
        {
            var Q0;
            Q0=qCreatedBy(makeId("Front.planeOp"),FACE);
            var sketch = newSketch(context, id + "F68", { "sketchPlane" : qUnion([Q0])});
            skLineSegment(sketch, "E29.bottom", {"start": v(1.6, 4.04) * mm, "end": v(-1.6, 4.04) * mm});
            skLineSegment(sketch, "E29.top", {"start": v(1.6, 22.49) * mm, "end": v(-1.6, 22.49) * mm});
            skLineSegment(sketch, "E29.left", {"start": v(1.6, 4.04) * mm, "end": v(1.6, 22.49) * mm});
            skLineSegment(sketch, "E29.right", {"start": v(-1.6, 4.04) * mm, "end": v(-1.6, 22.49) * mm});
            skPoint(sketch, "E29.middle", {"position": v(0, 13.26) * mm});
            skSolve(sketch);
        }
        {
            var Q0;
            Q0 = qSketchRegion(id + "F68", true);
            extrude(context, id + "F69", {"entities" : qUnion([Q0]), "operationType" : NewBodyOperationType.REMOVE, "depth" : 72 * mm});
        }
        {
            var Q0;
            Q0=qCreatedBy(makeId("Front.planeOp"),FACE);
            var sketch = newSketch(context, id + "F70", { "sketchPlane" : qUnion([Q0])});
            skLineSegment(sketch, "E30.bottom", {"start": v(1.45, 4.28) * mm, "end": v(-1.45, 4.28) * mm});
            skLineSegment(sketch, "E30.top", {"start": v(1.45, 22.15) * mm, "end": v(-1.45, 22.15) * mm});
            skLineSegment(sketch, "E30.left", {"start": v(1.45, 4.28) * mm, "end": v(1.45, 22.15) * mm});
            skLineSegment(sketch, "E30.right", {"start": v(-1.45, 4.28) * mm, "end": v(-1.45, 22.15) * mm});
            skPoint(sketch, "E30.middle", {"position": v(0, 13.22) * mm});
            skSolve(sketch);
        }
        {
            var Q0;
            Q0 = qSketchRegion(id + "F70", true);
            extrude(context, id + "F71", {"entities" : qUnion([Q0]), "operationType" : NewBodyOperationType.ADD, "oppositeDirection" : true, "depth" : 37.4 * mm});
        }
        {
            var Q0;
            Q0=qCreatedBy(makeId("Right.planeOp"),FACE);
            var sketch = newSketch(context, id + "F72", { "sketchPlane" : qUnion([Q0])});
            skEllipse(sketch, "E31", {"center": v(-44.6, 25.75) * mm, "majorRadius": 9.82 * mm, "minorRadius": 5.15 * mm, "majorAxis": v(1, 0)});
            skSolve(sketch);
        }
        {
            var Q0;
            Q0 = qSketchRegion(id + "F72", true);
            extrude(context, id + "F73", {"entities" : qUnion([Q0]), "operationType" : NewBodyOperationType.REMOVE, "oppositeDirection" : true, "depth" : 25 * mm});
        }
        {
            var Q0;
            Q0=qCreatedBy(makeId("Right.planeOp"),FACE);
            var sketch = newSketch(context, id + "F74", { "sketchPlane" : qUnion([Q0])});
            skEllipse(sketch, "E32", {"center": v(-12.97, 25.73) * mm, "majorRadius": 8.4 * mm, "minorRadius": 5.54 * mm, "majorAxis": v(1, 0)});
            skSolve(sketch);
        }
        {
            var Q0;
            Q0 = qSketchRegion(id + "F74", true);
            extrude(context, id + "F75", {"entities" : qUnion([Q0]), "operationType" : NewBodyOperationType.REMOVE, "oppositeDirection" : true, "depth" : 25 * mm});
        }
        {
            var Q0;
            Q0=qCreatedBy(makeId("Right.planeOp"),FACE);
            var sketch = newSketch(context, id + "F76", { "sketchPlane" : qUnion([Q0])});
            skEllipse(sketch, "E33", {"center": v(5.86, 25.4) * mm, "majorRadius": 7.99 * mm, "minorRadius": 5.12 * mm, "majorAxis": v(1, 0)});
            skSolve(sketch);
        }
        {
            var Q0;
            Q0=qCreatedBy(makeId("Right.planeOp"),FACE);
            var sketch = newSketch(context, id + "F77", { "sketchPlane" : qUnion([Q0])});
            skEllipse(sketch, "E34", {"center": v(5.85, 25.43) * mm, "majorRadius": 7.99 * mm, "minorRadius": 5.12 * mm, "majorAxis": v(1, 0)});
            skSolve(sketch);
        }
        {
            var Q0;
            Q0 = qSketchRegion(id + "F76", true);
            extrude(context, id + "F78", {"entities" : qUnion([Q0]), "operationType" : NewBodyOperationType.REMOVE, "oppositeDirection" : true, "depth" : 25 * mm});
        }
        {
            var Q0;
            Q0 = qSketchRegion(id + "F77", true);
            extrude(context, id + "F79", {"entities" : qUnion([Q0]), "operationType" : NewBodyOperationType.REMOVE, "depth" : 25 * mm});
        }
        {
            var Q0;
            Q0=qCreatedBy(makeId("Right.planeOp"),FACE);
            var sketch = newSketch(context, id + "F80", { "sketchPlane" : qUnion([Q0])});
            skEllipse(sketch, "E35", {"center": v(24.26, 25.5) * mm, "majorRadius": 8.18 * mm, "minorRadius": 5.09 * mm, "majorAxis": v(1, 0)});
            skSolve(sketch);
        }
        {
            var Q0;
            Q0=qCreatedBy(makeId("Right.planeOp"),FACE);
            var sketch = newSketch(context, id + "F81", { "sketchPlane" : qUnion([Q0])});
            skEllipse(sketch, "E36", {"center": v(24.27, 25.5) * mm, "majorRadius": 8.18 * mm, "minorRadius": 5.09 * mm, "majorAxis": v(1, 0)});
            skSolve(sketch);
        }
        {
            var Q0;
            Q0 = qSketchRegion(id + "F80", true);
            extrude(context, id + "F82", {"entities" : qUnion([Q0]), "operationType" : NewBodyOperationType.REMOVE, "oppositeDirection" : true, "depth" : 25 * mm});
        }
        {
            var Q0;
            Q0 = qSketchRegion(id + "F81", true);
            extrude(context, id + "F83", {"entities" : qUnion([Q0]), "operationType" : NewBodyOperationType.REMOVE, "depth" : 25 * mm});
        }
    });
